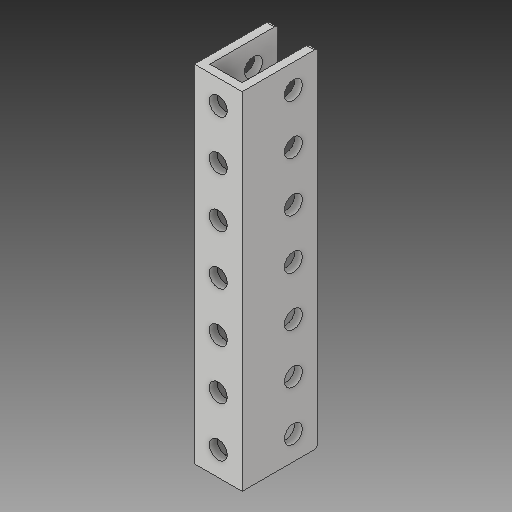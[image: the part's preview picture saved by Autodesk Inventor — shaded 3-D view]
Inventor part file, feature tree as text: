
AUTODESK INVENTOR PART (.ipt)
format: ipt  version: 2017 (Build 210142000, 142)  size: 157,696 bytes
history: native  units: in
note: dims shown in document units (in); Inventor stores cm internally (conversion verified against a paired STEP export)
features: fillet x1
ambient origin geometry x8: Origin, YZ Plane, XZ Plane, XY Plane, X Axis, Y Axis, Z Axis, Center Point
bodies: Solid1 (feature_tree)
feature tree (1):
  fillet  "Fillet1"  [1 undecoded]
note: 1 required parameter value undecoded (feature->parameter linkage not recoverable at this tier; creation-order binding heuristic only, values carry confidence <= 0.55)
